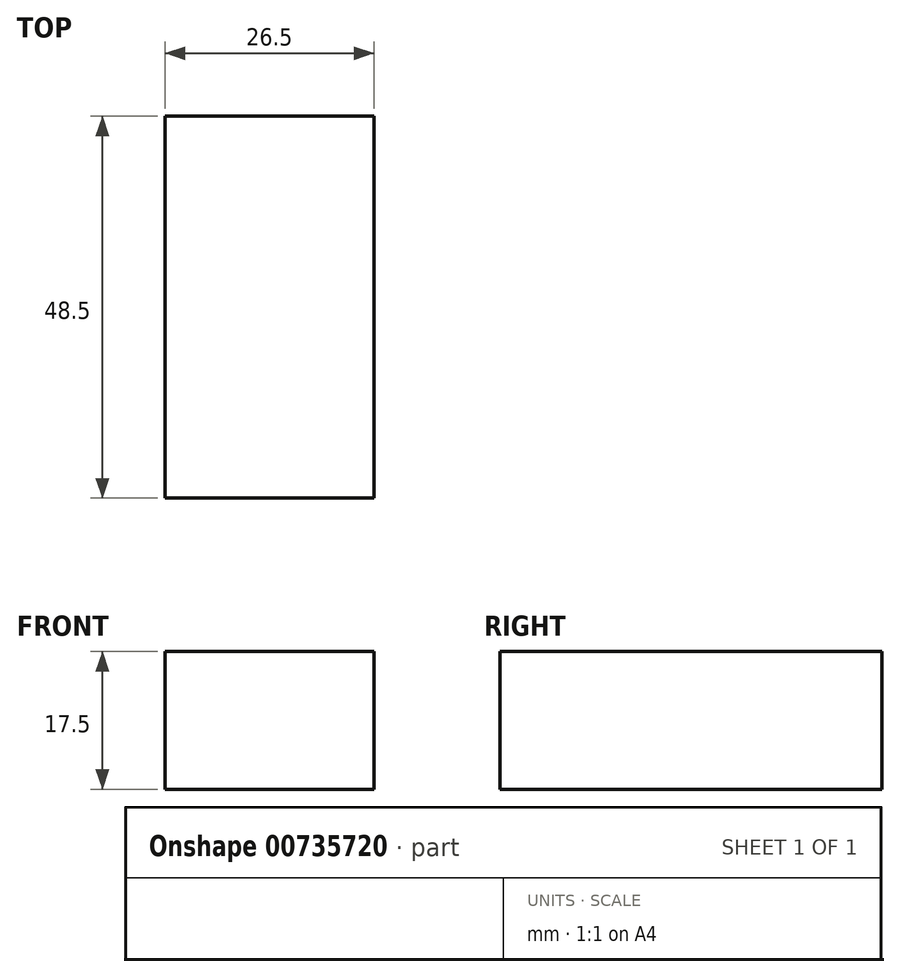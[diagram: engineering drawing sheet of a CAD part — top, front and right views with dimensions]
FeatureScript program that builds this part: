
annotation { "Feature Type Name" : "Feature", "Feature Type Description" : "" }
export const myFeature = defineFeature(function(context is Context, id is Id, definition is map)
    precondition{}
    {
        {
            var Q0;
            Q0=qCreatedBy(makeId("Top.planeOp"),FACE);
            var sketch = newSketch(context, id + "F0", { "sketchPlane" : qUnion([Q0])});
            skPoint(sketch, "E0", {"position": v(-13.25, 24.25) * mm});
            skLineSegment(sketch, "E1.bottom", {"start": v(-13.25, 24.25) * mm, "end": v(13.25, 24.25) * mm});
            skLineSegment(sketch, "E1.top", {"start": v(-13.25, -24.25) * mm, "end": v(13.25, -24.25) * mm});
            skLineSegment(sketch, "E1.left", {"start": v(-13.25, 24.25) * mm, "end": v(-13.25, -24.25) * mm});
            skLineSegment(sketch, "E1.right", {"start": v(13.25, 24.25) * mm, "end": v(13.25, -24.25) * mm});
            skLineSegment(sketch, "E2", {"start": v(-13.25, 0) * mm, "end": v(0, 0) * mm});
            skPoint(sketch, "E2.endSnap0", {"position": v(0, 24.25) * mm});
            skSolve(sketch);
        }
        {
            var Q0;
            {var subQ3=sQuery(id+"F0.wireOp",EDGE,"E1.bottom");Q0=makeQuery(id+"F0.imprint","IMPRINT",FACE,{"disambiguationData":[TD([[makeQuery(id+"F0.imprint","IMPRINT",EDGE,{"derivedFrom":subQ3}),-1.0]])]});}
            extrude(context, id + "F1", {"entities" : qUnion([Q0]), "depth" : 17.5 * mm, "offsetDistance" : 25.4 * mm});
        }
    });
